# Revit family: LAMP_KOMBIC 150 SURFACE 3500 CRI80 OPAL DALI
name_source: partatom
category: Luminarias
revit_build: Autodesk Revit 2018 (Build: 20190510_1515(x64)
units: mm (PartAtom-declared; Revit-internal decimal feet)

## family parameters
Anfitrión = Cara
Compartido = No
Corte con vacíos al cargar = No
Cota de conector redondo = Diámetro de uso
Origen de luz = Sí
Punto de cálculo de habitación = No
Tipo de pieza = Normal

## types (12) — shared parameters
CRI = 80
Cambio de temperatura de color de luz atenuada = <Ninguno>
Diameter = 150 mm
Elevación por defecto = 1219 mm
Fabricante = LAMP
Filtro de color = 16777215
Gear = Adjustable DALI
Height = 180 mm  [stored 0.590551 ft]
IEE = A+
Installation instructions = https://www.lamp.es
Insulation class = II
LED Lifetime = 50.000 L80 B10
Lamp = COB LED
Last update = 02/09/2021
Luminaire type = Suspended
MacAdam = 3
Manufacturer URL = http://www.lamp.es
Manufacturer country = Spain
Manufacturer name = LAMP
Material cable suspension = LAMP_Acero genérico
Material difusor = LAMP_PMMA Difusor Kombic
Model explanation = Possibility of chossing between surface or suspended within the model
Plum = 28 W
Power = 25 W
Power Supply = 220-240V 50/60Hz
Product URL = https://www.lamp.es
Product datasheet = http://www.lamp.es
Protection rating = IP40
Type = COB PHILIPS
Weight = 1.48 kg
Ángulo de inclinación = -90.00°

## per-type parameters (varying)
| type | Archivo de red fotométrica | Efficacy | Finish | Material cuerpo | Material floron | Material reflector | Modelo | Product code |
| 2673LM 3000K  M/B | K21SF3540OP830NMB.IES | 96 lm/W | Matte black RAL 9011 | LAMP_Plástico genérico NG | LAMP_Plástico genérico NG | LAMP_PC Reflector Kombic Metalizado Mate | K21SF3540OP830DMB | K21SF3540OP830DMB |
| 2673LM 3000K  M/W | K21SF3540OP830NMW.IES | 96 lm/W | Matte white RAL 9010 | LAMP_Plástico genérico BL | LAMP_Plástico genérico BL | LAMP_PC Reflector Kombic Metalizado Mate | K21SF3540OP830DMW | K21SF3540OP830DMW |
| 2759LM 3000K  W/B | K21SF3540OP830NWB.IES | 99 lm/W | Matte black RAL 9011 | LAMP_Plástico genérico NG | LAMP_Plástico genérico NG | LAMP_PC Reflector Kombic Blanco | K21SF3540OP830DWB | K21SF3540OP830DWB |
| 2759LM 3000K  W/W | K21SF3540OP830NWW.IES | 99 lm/W | Matte white RAL 9010 | LAMP_Plástico genérico BL | LAMP_Plástico genérico BL | LAMP_PC Reflector Kombic Blanco | K21SF3540OP830DWW | K21SF3540OP830DWW |
| 2784LM 4000K  M/B | K21SF3540OP840NMB.IES | 99 lm/W | Matte black RAL 9011 | LAMP_Plástico genérico NG | LAMP_Plástico genérico NG | LAMP_PC Reflector Kombic Metalizado Mate | K21SF3540OP840DMB | K21SF3540OP840DMB |
| 2784LM 4000K  M/W | K21SF3540OP840NMW.IES | 99 lm/W | Matte white RAL 9010 | LAMP_Plástico genérico BL | LAMP_Plástico genérico BL | LAMP_PC Reflector Kombic Metalizado Mate | K21SF3540OP840DMW | K21SF3540OP840DMW |
| 2788LM 3000K  BR/B | K21SF3540OP830NRB.IES | 100 lm/W | Matte black RAL 9011 | LAMP_Plástico genérico NG | LAMP_Plástico genérico NG | LAMP_PC Reflector Kombic Metalizado Brillante | K21SF3540OP830DRB | K21SF3540OP830DRB |
| 2788LM 3000K  BR/W | K21SF3540OP830NRW.IES | 100 lm/W | Matte white RAL 9010 | LAMP_Plástico genérico BL | LAMP_Plástico genérico BL | LAMP_PC Reflector Kombic Metalizado Brillante | K21SF3540OP830DRW | K21SF3540OP830DRW |
| 2874LM 4000K  W/B | K21SF3540OP840NWB.IES | 103 lm/W | Matte black RAL 9011 | LAMP_Plástico genérico NG | LAMP_Plástico genérico NG | LAMP_PC Reflector Kombic Blanco | K21SF3540OP840DWB | K21SF3540OP840DWB |
| 2874LM 4000K  W/W | K21SF3540OP840NWW.IES | 103 lm/W | Matte white RAL 9010 | LAMP_Plástico genérico BL | LAMP_Plástico genérico BL | LAMP_PC Reflector Kombic Blanco | K21SF3540OP840DWW | K21SF3540OP840DWW |
| 2904LM 4000K  BR/B | K21SF3540OP840NRB.IES | 104 lm/W | Matte black RAL 9011 | LAMP_Plástico genérico NG | LAMP_Plástico genérico NG | LAMP_PC Reflector Kombic Metalizado Brillante | K21SF3540OP840DRB | K21SF3540OP840DRB |
| 2904LM 4000K  BR/W | K21SF3540OP840NRW.IES | 104 lm/W | Matte white RAL 9010 | LAMP_Plástico genérico BL | LAMP_Plástico genérico BL | LAMP_PC Reflector Kombic Metalizado Brillante | K21SF3540OP840DRW | K21SF3540OP840DRW |

note: [stored X ft] marks values corroborated as IEEE doubles in the binary element streams (Revit-internal decimal feet)
